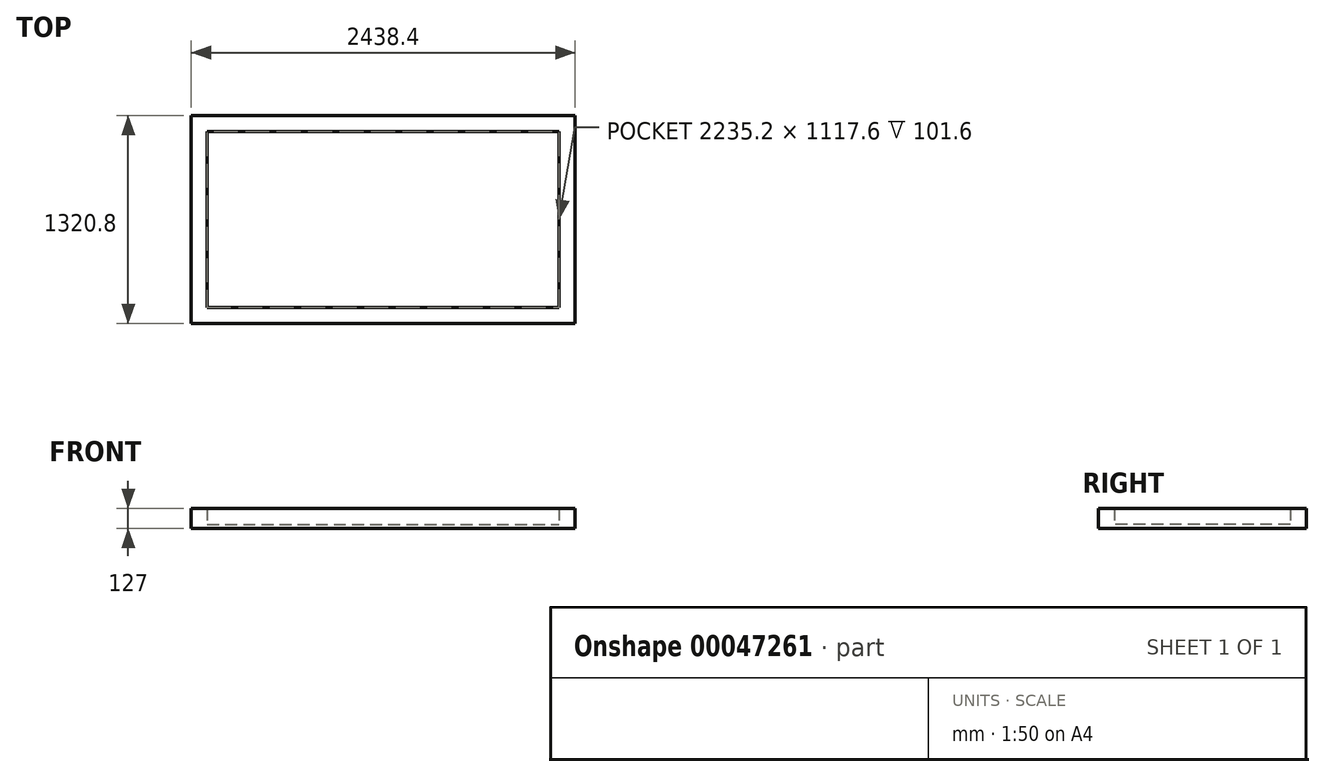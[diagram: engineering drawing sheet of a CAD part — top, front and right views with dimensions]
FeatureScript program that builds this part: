
annotation { "Feature Type Name" : "Feature", "Feature Type Description" : "" }
export const myFeature = defineFeature(function(context is Context, id is Id, definition is map)
    precondition{}
    {
        {
            var Q0;
            Q0=qCreatedBy(makeId("Top.planeOp"),FACE);
            var sketch = newSketch(context, id + "F0", { "sketchPlane" : qUnion([Q0])});
            skLineSegment(sketch, "E0.bottom", {"start": v(-1117.6, 558.8) * mm, "end": v(1117.6, 558.8) * mm});
            skLineSegment(sketch, "E0.top", {"start": v(-1117.6, -558.8) * mm, "end": v(1117.6, -558.8) * mm});
            skLineSegment(sketch, "E0.left", {"start": v(-1117.6, 558.8) * mm, "end": v(-1117.6, -558.8) * mm});
            skLineSegment(sketch, "E0.right", {"start": v(1117.6, 558.8) * mm, "end": v(1117.6, -558.8) * mm});
            skLineSegment(sketch, "E1.bottom", {"start": v(-1219.2, 660.4) * mm, "end": v(1219.2, 660.4) * mm});
            skLineSegment(sketch, "E1.top", {"start": v(-1219.2, -660.4) * mm, "end": v(1219.2, -660.4) * mm});
            skLineSegment(sketch, "E1.left", {"start": v(-1219.2, 660.4) * mm, "end": v(-1219.2, -660.4) * mm});
            skLineSegment(sketch, "E1.right", {"start": v(1219.2, 660.4) * mm, "end": v(1219.2, -660.4) * mm});
            skSolve(sketch);
        }
        {
            var Q0;
            Q0=makeQuery(id+"F0.imprint","IMPRINT",FACE,{"disambiguationData":[TD([[makeQuery(id+"F0.imprint","IMPRINT",EDGE,{"derivedFrom":sQuery(id+"F0.wireOp",EDGE,"E0.bottom")}),1.0]])]});
            var Q1;
            Q1=makeQuery(id+"F0.imprint","IMPRINT",FACE,{"disambiguationData":[TD([[makeQuery(id+"F0.imprint","IMPRINT",EDGE,{"derivedFrom":sQuery(id+"F0.wireOp",EDGE,"E0.bottom")}),-1.0]])]});
            extrude(context, id + "F1", {"entities" : qUnion([Q0, Q1]), "depth" : 25.4 * mm});
        }
        {
            var Q0;
            Q0=makeQuery(id+"F1.opExtrude","CAP_FACE",FACE,{"disambiguationData":[OSD([sQuery(id+"F0.wireOp",EDGE,"E1.bottom"),sQuery(id+"F0.wireOp",EDGE,"E1.top"),sQuery(id+"F0.wireOp",EDGE,"E1.left"),sQuery(id+"F0.wireOp",EDGE,"E1.right")])],"isStart":false});
            var sketch = newSketch(context, id + "F2", { "sketchPlane" : qUnion([Q0])});
            skLineSegment(sketch, "E2.0", {"start": v(1219.2, 660.4) * mm, "end": v(1219.2, -660.4) * mm});
            skLineSegment(sketch, "E3.0", {"start": v(-1219.2, 660.4) * mm, "end": v(1219.2, 660.4) * mm});
            skLineSegment(sketch, "E4.bottom", {"start": v(-1117.6, 558.8) * mm, "end": v(1117.6, 558.8) * mm});
            skLineSegment(sketch, "E4.top", {"start": v(-1117.6, -558.8) * mm, "end": v(1117.6, -558.8) * mm});
            skLineSegment(sketch, "E4.left", {"start": v(-1117.6, 558.8) * mm, "end": v(-1117.6, -558.8) * mm});
            skLineSegment(sketch, "E4.right", {"start": v(1117.6, 558.8) * mm, "end": v(1117.6, -558.8) * mm});
            skSolve(sketch);
        }
        {
            var Q0;
            Q0=makeQuery(id+"F2.imprint","IMPRINT",FACE,{"disambiguationData":[TD([[makeQuery(id+"F2.imprint","IMPRINT",EDGE,{"derivedFrom":sQuery(id+"F2.wireOp",EDGE,"E2.0")}),-1.0]])]});
            extrude(context, id + "F3", {"entities" : qUnion([Q0]), "operationType" : NewBodyOperationType.ADD, "depth" : 101.6 * mm});
        }
    });
